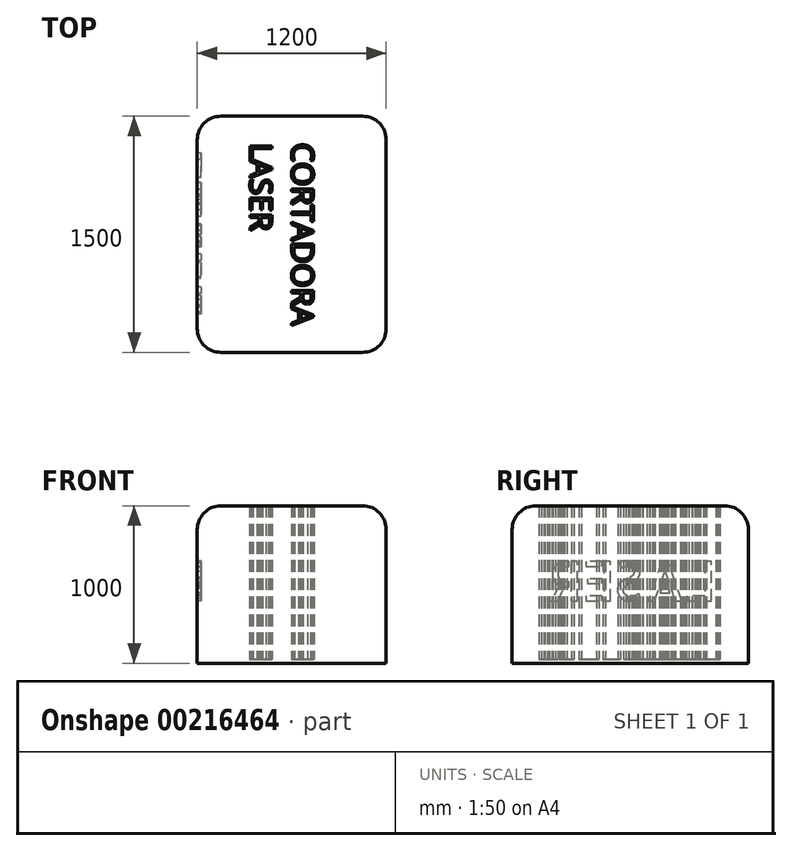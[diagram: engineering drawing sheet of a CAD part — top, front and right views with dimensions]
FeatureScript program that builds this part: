
annotation { "Feature Type Name" : "Feature", "Feature Type Description" : "" }
export const myFeature = defineFeature(function(context is Context, id is Id, definition is map)
    precondition{}
    {
        {
            var Q0;
            Q0=qCreatedBy(makeId("Top.planeOp"),FACE);
            var sketch = newSketch(context, id + "F0", { "sketchPlane" : qUnion([Q0])});
            skLineSegment(sketch, "E0.bottom", {"start": v(25.28, 19.07) * mm, "end": v(1225.28, 19.07) * mm});
            skLineSegment(sketch, "E0.top", {"start": v(25.28, 1519.07) * mm, "end": v(1225.28, 1519.07) * mm});
            skLineSegment(sketch, "E0.left", {"start": v(25.28, 19.07) * mm, "end": v(25.28, 1519.07) * mm});
            skLineSegment(sketch, "E0.right", {"start": v(1225.28, 19.07) * mm, "end": v(1225.28, 1519.07) * mm});
            skText(sketch, "E1", { "text": "CORTADORA\nLASER", "fontName": "OpenSans-Regular.ttf"});
            const initialGuessF0  = {"E1": [0.62465, 1.34976, 0, -1, 0.14]};
            skSetInitialGuess(sketch, initialGuessF0);
            skSolve(sketch);
        }
        {
            var Q0;
            Q0=qCreatedBy(makeId("Top.planeOp"),FACE);
            var sketch = newSketch(context, id + "F1", { "sketchPlane" : qUnion([Q0])});
            skLineSegment(sketch, "E2.bottom", {"start": v(25.28, 19.07) * mm, "end": v(1225.28, 19.07) * mm});
            skLineSegment(sketch, "E2.top", {"start": v(25.28, 1519.07) * mm, "end": v(1225.28, 1519.07) * mm});
            skLineSegment(sketch, "E2.left", {"start": v(25.28, 19.07) * mm, "end": v(25.28, 1519.07) * mm});
            skLineSegment(sketch, "E2.right", {"start": v(1225.28, 19.07) * mm, "end": v(1225.28, 1519.07) * mm});
            skSolve(sketch);
        }
        {
            var Q0;
            Q0=makeQuery(id+"F1.imprint","IMPRINT",FACE,{"disambiguationData":[TD([[makeQuery(id+"F1.imprint","IMPRINT",EDGE,{"derivedFrom":sQuery(id+"F1.wireOp",EDGE,"E2.bottom")}),1.0]])]});
            extrude(context, id + "F2", {"entities" : qUnion([Q0]), "depth" : 25 * mm});
        }
        {
            var Q0;
            Q0=makeQuery(id+"F0.imprint","IMPRINT",FACE,{"disambiguationData":[TD([[makeQuery(id+"F0.imprint","IMPRINT",EDGE,{"derivedFrom":sQuery(id+"F0.wireOp",EDGE,"E0.bottom")}),1.0]])]});
            var Q1;
            Q1=makeQuery(id+"F0.imprint","IMPRINT",FACE,{"disambiguationData":[TD([[makeQuery(id+"F0.imprint","IMPRINT",EDGE,{"derivedFrom":sQuery(id+"F0.wireOp",EDGE,"E1.sketch_text.stroke-23")}),1.0]])]});
            var Q2;
            Q2=makeQuery(id+"F0.imprint","IMPRINT",FACE,{"disambiguationData":[TD([[makeQuery(id+"F0.imprint","IMPRINT",EDGE,{"derivedFrom":sQuery(id+"F0.wireOp",EDGE,"E1.sketch_text.stroke-42")}),1.0]])]});
            var Q3;
            Q3=makeQuery(id+"F0.imprint","IMPRINT",FACE,{"disambiguationData":[TD([[makeQuery(id+"F0.imprint","IMPRINT",EDGE,{"derivedFrom":sQuery(id+"F0.wireOp",EDGE,"E1.sketch_text.stroke-145")}),1.0]])]});
            var Q4;
            Q4=makeQuery(id+"F0.imprint","IMPRINT",FACE,{"disambiguationData":[TD([[makeQuery(id+"F0.imprint","IMPRINT",EDGE,{"derivedFrom":sQuery(id+"F0.wireOp",EDGE,"E1.sketch_text.stroke-198")}),1.0]])]});
            var Q5;
            Q5=makeQuery(id+"F0.imprint","IMPRINT",FACE,{"disambiguationData":[TD([[makeQuery(id+"F0.imprint","IMPRINT",EDGE,{"derivedFrom":sQuery(id+"F0.wireOp",EDGE,"E1.sketch_text.stroke-92")}),1.0]])]});
            var Q6;
            Q6=makeQuery(id+"F0.imprint","IMPRINT",FACE,{"disambiguationData":[TD([[makeQuery(id+"F0.imprint","IMPRINT",EDGE,{"derivedFrom":sQuery(id+"F0.wireOp",EDGE,"E1.sketch_text.stroke-111")}),1.0]])]});
            var Q7;
            Q7=makeQuery(id+"F0.imprint","IMPRINT",FACE,{"disambiguationData":[TD([[makeQuery(id+"F0.imprint","IMPRINT",EDGE,{"derivedFrom":sQuery(id+"F0.wireOp",EDGE,"E1.sketch_text.stroke-77")}),1.0]])]});
            var Q8;
            Q8=makeQuery(id+"F0.imprint","IMPRINT",FACE,{"disambiguationData":[TD([[makeQuery(id+"F0.imprint","IMPRINT",EDGE,{"derivedFrom":sQuery(id+"F0.wireOp",EDGE,"E1.sketch_text.stroke-65")}),1.0]])]});
            var Q9;
            Q9=makeQuery(id+"F0.imprint","IMPRINT",FACE,{"disambiguationData":[TD([[makeQuery(id+"F0.imprint","IMPRINT",EDGE,{"derivedFrom":sQuery(id+"F0.wireOp",EDGE,"E1.sketch_text.stroke-126")}),1.0]])]});
            extrude(context, id + "F3", {"entities" : qUnion([Q0, Q1, Q2, Q3, Q4, Q5, Q6, Q7, Q8, Q9]), "operationType" : NewBodyOperationType.ADD, "depth" : 1000 * mm, "hasSecondDirection" : true, "secondDirectionOppositeDirection" : false, "secondDirectionDepth" : 25 * mm});
        }
        {
            var Q0;
            Q0=makeQuery(id+"F3.opExtrude","CAP_EDGE",EDGE,{"disambiguationData":[OSD([sQuery(id+"F0.wireOp",EDGE,"E0.right")])],"isStart":false});
            var Q1;
            Q1=makeQuery(id+"F3.opExtrude","CAP_EDGE",EDGE,{"disambiguationData":[OSD([sQuery(id+"F0.wireOp",EDGE,"E0.left")])],"isStart":false});
            var Q2;
            Q2=makeQuery(id+"F3.opExtrude","CAP_EDGE",EDGE,{"disambiguationData":[OSD([sQuery(id+"F0.wireOp",EDGE,"E0.top")])],"isStart":false});
            var Q3;
            Q3=makeQuery(id+"F3.opExtrude","CAP_EDGE",EDGE,{"disambiguationData":[OSD([sQuery(id+"F0.wireOp",EDGE,"E0.bottom")])],"isStart":false});
            var Q4;
            Q4=makeQuery(id+"F3.boolean.opBoolean","MERGE",EDGE,{"derivedFrom":[makeQuery(id+"F2.opExtrude","SWEPT_EDGE",EDGE,{"disambiguationData":[OSD([sQuery(id+"F1.wireOp",EDGE,"E2.bottom"),sQuery(id+"F1.wireOp",EDGE,"E2.left")])]}),makeQuery(id+"F3.opExtrude","SWEPT_EDGE",EDGE,{"disambiguationData":[OSD([sQuery(id+"F0.wireOp",EDGE,"E0.bottom"),sQuery(id+"F0.wireOp",EDGE,"E0.left")])]})]});
            var Q5;
            Q5=makeQuery(id+"F3.boolean.opBoolean","MERGE",EDGE,{"derivedFrom":[makeQuery(id+"F2.opExtrude","SWEPT_EDGE",EDGE,{"disambiguationData":[OSD([sQuery(id+"F1.wireOp",EDGE,"E2.top"),sQuery(id+"F1.wireOp",EDGE,"E2.left")])]}),makeQuery(id+"F3.opExtrude","SWEPT_EDGE",EDGE,{"disambiguationData":[OSD([sQuery(id+"F0.wireOp",EDGE,"E0.top"),sQuery(id+"F0.wireOp",EDGE,"E0.left")])]})]});
            var Q6;
            Q6=makeQuery(id+"F3.boolean.opBoolean","MERGE",EDGE,{"derivedFrom":[makeQuery(id+"F2.opExtrude","SWEPT_EDGE",EDGE,{"disambiguationData":[OSD([sQuery(id+"F1.wireOp",EDGE,"E2.bottom"),sQuery(id+"F1.wireOp",EDGE,"E2.right")])]}),makeQuery(id+"F3.opExtrude","SWEPT_EDGE",EDGE,{"disambiguationData":[OSD([sQuery(id+"F0.wireOp",EDGE,"E0.bottom"),sQuery(id+"F0.wireOp",EDGE,"E0.right")])]})]});
            var Q7;
            Q7=makeQuery(id+"F3.boolean.opBoolean","MERGE",EDGE,{"derivedFrom":[makeQuery(id+"F2.opExtrude","SWEPT_EDGE",EDGE,{"disambiguationData":[OSD([sQuery(id+"F1.wireOp",EDGE,"E2.top"),sQuery(id+"F1.wireOp",EDGE,"E2.right")])]}),makeQuery(id+"F3.opExtrude","SWEPT_EDGE",EDGE,{"disambiguationData":[OSD([sQuery(id+"F0.wireOp",EDGE,"E0.top"),sQuery(id+"F0.wireOp",EDGE,"E0.right")])]})]});
            fillet(context, id + "F4", {"entities" : qUnion([Q0, Q1, Q2, Q3, Q4, Q5, Q6, Q7]), "radius" : 150 * mm, "tangentPropagation" : true, "allowEdgeOverflow" : false});
        }
        {
            var Q0;
            Q0=makeQuery(id+"F3.boolean.opBoolean","MERGE",FACE,{"derivedFrom":[makeQuery(id+"F2.opExtrude","SWEPT_FACE",FACE,{"disambiguationData":[OSD([sQuery(id+"F1.wireOp",EDGE,"E2.left")])]}),makeQuery(id+"F3.opExtrude","SWEPT_FACE",FACE,{"disambiguationData":[OSD([sQuery(id+"F0.wireOp",EDGE,"E0.left")])]})]});
            var sketch = newSketch(context, id + "F5", { "sketchPlane" : qUnion([Q0])});
            skText(sketch, "E3", { "text": "LASER", "fontName": "AllertaStencil-Regular.ttf"});
            const initialGuessF5  = {"E3": [-1.3159, 0.39624, 1, 0, 0.25]};
            skSetInitialGuess(sketch, initialGuessF5);
            skSolve(sketch);
        }
        {
            var Q0;
            Q0 = qSketchRegion(id + "F5", true);
            extrude(context, id + "F6", {"entities" : qUnion([Q0]), "operationType" : NewBodyOperationType.REMOVE, "oppositeDirection" : true, "depth" : 25 * mm});
        }
    });
